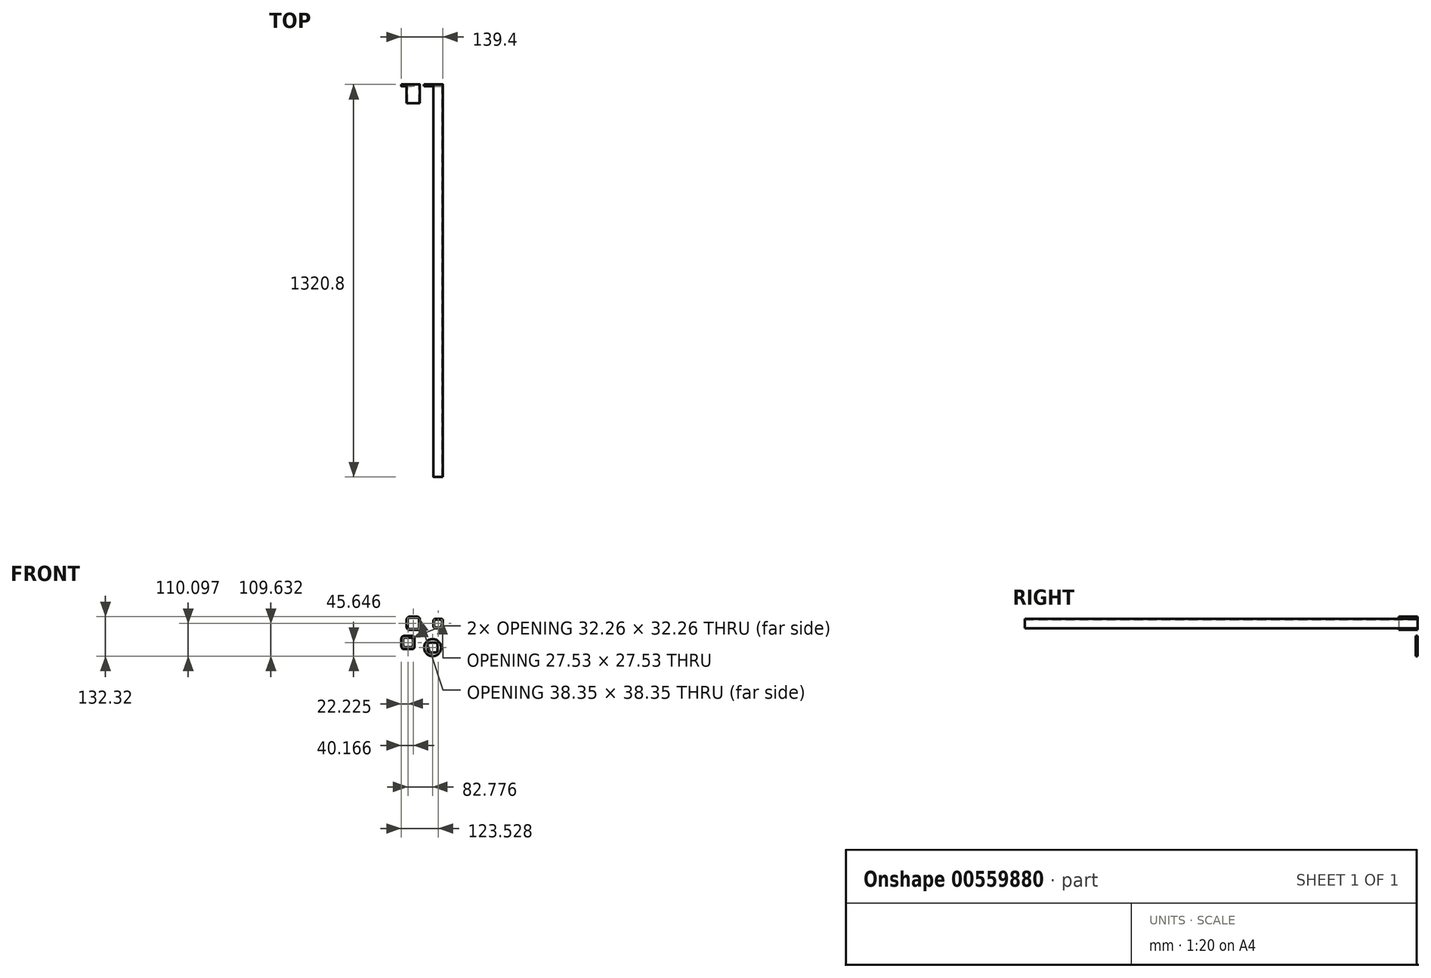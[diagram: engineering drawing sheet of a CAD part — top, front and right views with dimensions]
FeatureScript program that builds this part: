
annotation { "Feature Type Name" : "Feature", "Feature Type Description" : "" }
export const myFeature = defineFeature(function(context is Context, id is Id, definition is map)
    precondition{}
    {
        {
            var Q0;
            Q0=qCreatedBy(makeId("Front.planeOp"),FACE);
            var sketch = newSketch(context, id + "F0", { "sketchPlane" : qUnion([Q0])});
            skLineSegment(sketch, "E0.bottom", {"start": v(-62.7, 67.52) * mm, "end": v(-36.53, 67.52) * mm});
            skLineSegment(sketch, "E0.top", {"start": v(-62.7, 23.07) * mm, "end": v(-36.53, 23.07) * mm});
            skLineSegment(sketch, "E0.left", {"start": v(-71.84, 58.38) * mm, "end": v(-71.84, 32.22) * mm});
            skLineSegment(sketch, "E0.right", {"start": v(-27.39, 58.38) * mm, "end": v(-27.39, 32.22) * mm});
            skLineSegment(sketch, "E1.0", {"start": v(-62.7, 64.47) * mm, "end": v(-36.53, 64.47) * mm});
            skLineSegment(sketch, "E1.1", {"start": v(-68.8, 58.38) * mm, "end": v(-68.8, 32.22) * mm});
            skLineSegment(sketch, "E1.2", {"start": v(-62.7, 26.12) * mm, "end": v(-36.53, 26.12) * mm});
            skLineSegment(sketch, "E1.3", {"start": v(-30.44, 58.38) * mm, "end": v(-30.44, 32.22) * mm});
            skPoint(sketch, "E2.visualSharp", {"position": v(-71.84, 67.52) * mm});
            skArc(sketch, "E2.filletArc", {"start": v(-62.7, 67.52) * mm, "mid": v(-69.16, 64.84) * mm, "end": v(-71.84, 58.38) * mm});
            skPoint(sketch, "E3.visualSharp", {"position": v(-68.8, 64.47) * mm});
            skArc(sketch, "E4.0", {"start": v(-62.7, 64.47) * mm, "mid": v(-67, 62.69) * mm, "end": v(-68.8, 58.38) * mm});
            skLineSegment(sketch, "E5", {"start": v(-49.61, 26.12) * mm, "end": v(-49.61, 64.47) * mm, "construction": true});
            skLineSegment(sketch, "E6", {"start": v(-30.44, 45.3) * mm, "end": v(-68.8, 45.3) * mm, "construction": true});
            skPoint(sketch, "E6.endSnap0", {"position": v(-68.8, 42.25) * mm});
            skArc(sketch, "E7.MirrorCS", {"start": v(-36.53, 64.47) * mm, "mid": v(-32.22, 62.69) * mm, "end": v(-30.44, 58.38) * mm});
            skArc(sketch, "E8.MirrorCS", {"start": v(-36.53, 67.52) * mm, "mid": v(-30.07, 64.84) * mm, "end": v(-27.39, 58.38) * mm});
            skPoint(sketch, "E9.orphan", {"position": v(-30.44, 64.47) * mm});
            skArc(sketch, "E10.MirrorCS", {"start": v(-36.53, 26.12) * mm, "mid": v(-32.22, 27.9) * mm, "end": v(-30.44, 32.22) * mm});
            skArc(sketch, "E11.MirrorCS", {"start": v(-36.53, 23.07) * mm, "mid": v(-30.07, 25.75) * mm, "end": v(-27.39, 32.22) * mm});
            skArc(sketch, "E12.MirrorCS", {"start": v(-62.7, 23.07) * mm, "mid": v(-69.16, 25.75) * mm, "end": v(-71.84, 32.22) * mm});
            skArc(sketch, "E13.MirrorCS", {"start": v(-62.7, 26.12) * mm, "mid": v(-67, 27.9) * mm, "end": v(-68.8, 32.22) * mm});
            skPoint(sketch, "E14.orphan", {"position": v(-71.84, 23.07) * mm});
            skPoint(sketch, "E15.orphan", {"position": v(-68.8, 26.12) * mm});
            skPoint(sketch, "E16.orphan", {"position": v(-30.44, 26.12) * mm});
            skSolve(sketch);
        }
        {
            var Q0;
            Q0=makeQuery(id+"F0.imprint","IMPRINT",FACE,{"disambiguationData":[TD([[makeQuery(id+"F0.imprint","IMPRINT",EDGE,{"derivedFrom":sQuery(id+"F0.wireOp",EDGE,"E0.bottom")}),-1.0]])]});
            extrude(context, id + "F1", {"entities" : qUnion([Q0]), "depth" : 63.5 * mm, "offsetDistance" : 25.4 * mm});
        }
        {
            var Q0;
            Q0=qCreatedBy(makeId("Front.planeOp"),FACE);
            var sketch = newSketch(context, id + "F2", { "sketchPlane" : qUnion([Q0])});
            skLineSegment(sketch, "E17.bottom", {"start": v(24.2, 60.7) * mm, "end": v(43.3, 60.7) * mm});
            skLineSegment(sketch, "E17.top", {"start": v(24.2, 28.96) * mm, "end": v(43.3, 28.96) * mm});
            skLineSegment(sketch, "E17.left", {"start": v(17.87, 54.38) * mm, "end": v(17.87, 35.28) * mm});
            skLineSegment(sketch, "E17.right", {"start": v(49.62, 54.38) * mm, "end": v(49.62, 35.28) * mm});
            skPoint(sketch, "E18.visualSharp", {"position": v(17.87, 60.7) * mm});
            skArc(sketch, "E18.filletArc", {"start": v(24.2, 60.7) * mm, "mid": v(19.73, 58.85) * mm, "end": v(17.87, 54.38) * mm});
            skPoint(sketch, "E19.visualSharp", {"position": v(49.62, 60.7) * mm});
            skArc(sketch, "E19.filletArc", {"start": v(49.62, 54.38) * mm, "mid": v(47.77, 58.85) * mm, "end": v(43.3, 60.7) * mm});
            skPoint(sketch, "E20.visualSharp", {"position": v(49.62, 28.96) * mm});
            skArc(sketch, "E20.filletArc", {"start": v(43.3, 28.96) * mm, "mid": v(47.77, 30.8) * mm, "end": v(49.62, 35.28) * mm});
            skPoint(sketch, "E21.visualSharp", {"position": v(17.87, 28.96) * mm});
            skArc(sketch, "E21.filletArc", {"start": v(17.87, 35.28) * mm, "mid": v(19.73, 30.8) * mm, "end": v(24.2, 28.96) * mm});
            skLineSegment(sketch, "E22.0", {"start": v(24.2, 58.6) * mm, "end": v(43.3, 58.6) * mm});
            skArc(sketch, "E22.1", {"start": v(47.51, 54.38) * mm, "mid": v(46.28, 57.36) * mm, "end": v(43.3, 58.6) * mm});
            skArc(sketch, "E22.2", {"start": v(24.2, 58.6) * mm, "mid": v(21.22, 57.36) * mm, "end": v(19.98, 54.38) * mm});
            skLineSegment(sketch, "E22.3", {"start": v(47.51, 54.38) * mm, "end": v(47.51, 35.28) * mm});
            skLineSegment(sketch, "E22.4", {"start": v(19.98, 54.38) * mm, "end": v(19.98, 35.28) * mm});
            skArc(sketch, "E22.5", {"start": v(19.98, 35.28) * mm, "mid": v(21.22, 32.3) * mm, "end": v(24.2, 31.07) * mm});
            skLineSegment(sketch, "E22.6", {"start": v(24.2, 31.07) * mm, "end": v(43.3, 31.07) * mm});
            skArc(sketch, "E22.7", {"start": v(43.3, 31.07) * mm, "mid": v(46.28, 32.3) * mm, "end": v(47.51, 35.28) * mm});
            skSolve(sketch);
        }
        {
            var Q0;
            Q0=makeQuery(id+"F2.imprint","IMPRINT",FACE,{"disambiguationData":[TD([[makeQuery(id+"F2.imprint","IMPRINT",EDGE,{"derivedFrom":sQuery(id+"F2.wireOp",EDGE,"E17.bottom")}),-1.0]])]});
            extrude(context, id + "F3", {"entities" : qUnion([Q0]), "depth" : 1320.8 * mm, "offsetDistance" : 25.4 * mm});
        }
        {
            var Q0;
            Q0=qCreatedBy(makeId("Front.planeOp"),FACE);
            var sketch = newSketch(context, id + "F4", { "sketchPlane" : qUnion([Q0])});
            skPoint(sketch, "E23.visualSharp", {"position": v(-89.78, 2.96) * mm});
            skPoint(sketch, "E24.visualSharp", {"position": v(-87.62, 0.91) * mm});
            skLineSegment(sketch, "E25", {"start": v(-67.55, -39.22) * mm, "end": v(-67.55, 0.91) * mm, "construction": true});
            skLineSegment(sketch, "E26", {"start": v(-47.49, -19.15) * mm, "end": v(-87.62, -19.15) * mm, "construction": true});
            skPoint(sketch, "E26.endSnap0", {"position": v(-87.62, -23.3) * mm});
            skPoint(sketch, "E27.orphan", {"position": v(-47.49, 0.91) * mm});
            skPoint(sketch, "E28.orphan", {"position": v(-89.78, -41.5) * mm});
            skPoint(sketch, "E29.orphan", {"position": v(-87.62, -39.22) * mm});
            skPoint(sketch, "E30.orphan", {"position": v(-47.49, -39.22) * mm});
            skLineSegment(sketch, "E31.bottom", {"start": v(-77.1, -3.28) * mm, "end": v(-58, -3.28) * mm, "construction": true});
            skLineSegment(sketch, "E31.top", {"start": v(-77.1, -35.03) * mm, "end": v(-58, -35.03) * mm, "construction": true});
            skLineSegment(sketch, "E31.left", {"start": v(-83.43, -9.6) * mm, "end": v(-83.43, -28.7) * mm, "construction": true});
            skLineSegment(sketch, "E31.right", {"start": v(-51.68, -9.6) * mm, "end": v(-51.68, -28.7) * mm, "construction": true});
            skPoint(sketch, "E32.visualSharp", {"position": v(-83.43, -3.28) * mm});
            skArc(sketch, "E32.filletArc", {"start": v(-77.1, -3.28) * mm, "mid": v(-81.58, -5.13) * mm, "end": v(-83.43, -9.6) * mm, "construction": true});
            skPoint(sketch, "E33.visualSharp", {"position": v(-51.68, -3.28) * mm});
            skArc(sketch, "E33.filletArc", {"start": v(-51.68, -9.6) * mm, "mid": v(-53.53, -5.13) * mm, "end": v(-58, -3.28) * mm, "construction": true});
            skPoint(sketch, "E34.visualSharp", {"position": v(-51.68, -35.03) * mm});
            skArc(sketch, "E34.filletArc", {"start": v(-58, -35.03) * mm, "mid": v(-53.53, -33.18) * mm, "end": v(-51.68, -28.7) * mm, "construction": true});
            skPoint(sketch, "E35.visualSharp", {"position": v(-83.43, -35.03) * mm});
            skArc(sketch, "E35.filletArc", {"start": v(-83.43, -28.7) * mm, "mid": v(-81.58, -33.18) * mm, "end": v(-77.1, -35.03) * mm, "construction": true});
            skLineSegment(sketch, "E36", {"start": v(-51.68, -19.15) * mm, "end": v(-83.43, -19.15) * mm, "construction": true});
            skLineSegment(sketch, "E37", {"start": v(-67.55, -3.28) * mm, "end": v(-67.55, -35.03) * mm, "construction": true});
            skArc(sketch, "E38.0", {"start": v(-77.1, -3.02) * mm, "mid": v(-81.76, -4.95) * mm, "end": v(-83.68, -9.6) * mm});
            skLineSegment(sketch, "E38.1", {"start": v(-83.68, -9.6) * mm, "end": v(-83.68, -28.7) * mm});
            skLineSegment(sketch, "E38.2", {"start": v(-77.1, -3.02) * mm, "end": v(-58, -3.02) * mm});
            skArc(sketch, "E38.3", {"start": v(-83.68, -28.7) * mm, "mid": v(-81.76, -33.36) * mm, "end": v(-77.1, -35.28) * mm});
            skArc(sketch, "E38.4", {"start": v(-51.43, -9.6) * mm, "mid": v(-53.35, -4.95) * mm, "end": v(-58, -3.02) * mm});
            skLineSegment(sketch, "E38.5", {"start": v(-51.43, -9.6) * mm, "end": v(-51.43, -28.7) * mm});
            skArc(sketch, "E38.6", {"start": v(-58, -35.28) * mm, "mid": v(-53.35, -33.36) * mm, "end": v(-51.43, -28.7) * mm});
            skLineSegment(sketch, "E38.7", {"start": v(-77.1, -35.28) * mm, "end": v(-58, -35.28) * mm});
            skLineSegment(sketch, "E39.bottom", {"start": v(-80.64, 3.07) * mm, "end": v(-54.47, 3.07) * mm});
            skLineSegment(sketch, "E39.top", {"start": v(-80.64, -41.38) * mm, "end": v(-54.47, -41.38) * mm});
            skLineSegment(sketch, "E39.left", {"start": v(-89.78, -6.07) * mm, "end": v(-89.78, -32.23) * mm});
            skLineSegment(sketch, "E39.right", {"start": v(-45.33, -6.07) * mm, "end": v(-45.33, -32.23) * mm});
            skLineSegment(sketch, "E40.0", {"start": v(-80.64, 0.02) * mm, "end": v(-54.47, 0.02) * mm, "construction": true});
            skLineSegment(sketch, "E40.1", {"start": v(-86.73, -6.07) * mm, "end": v(-86.73, -32.23) * mm, "construction": true});
            skLineSegment(sketch, "E40.2", {"start": v(-80.64, -38.33) * mm, "end": v(-54.47, -38.33) * mm, "construction": true});
            skLineSegment(sketch, "E40.3", {"start": v(-48.38, -6.07) * mm, "end": v(-48.38, -32.23) * mm, "construction": true});
            skPoint(sketch, "E41.visualSharp", {"position": v(-89.78, 3.07) * mm});
            skArc(sketch, "E41.filletArc", {"start": v(-80.64, 3.07) * mm, "mid": v(-87.1, 0.4) * mm, "end": v(-89.78, -6.07) * mm});
            skPoint(sketch, "E42.visualSharp", {"position": v(-86.73, 0.02) * mm});
            skArc(sketch, "E43.0", {"start": v(-80.64, 0.02) * mm, "mid": v(-84.95, -1.76) * mm, "end": v(-86.73, -6.07) * mm, "construction": true});
            skLineSegment(sketch, "E44", {"start": v(-67.55, -38.33) * mm, "end": v(-67.55, 0.02) * mm, "construction": true});
            skLineSegment(sketch, "E45", {"start": v(-48.38, -19.15) * mm, "end": v(-86.73, -19.15) * mm, "construction": true});
            skPoint(sketch, "E45.endSnap0", {"position": v(-86.73, -22.2) * mm});
            skArc(sketch, "E46.MirrorCS", {"start": v(-54.47, 0.02) * mm, "mid": v(-50.16, -1.76) * mm, "end": v(-48.38, -6.07) * mm, "construction": true});
            skArc(sketch, "E47.MirrorCS", {"start": v(-54.47, 3.07) * mm, "mid": v(-48, 0.4) * mm, "end": v(-45.33, -6.07) * mm});
            skPoint(sketch, "E48.orphan", {"position": v(-48.38, 0.02) * mm});
            skArc(sketch, "E49.MirrorCS", {"start": v(-54.47, -38.33) * mm, "mid": v(-50.16, -36.55) * mm, "end": v(-48.38, -32.23) * mm, "construction": true});
            skArc(sketch, "E50.MirrorCS", {"start": v(-54.47, -41.38) * mm, "mid": v(-48, -38.7) * mm, "end": v(-45.33, -32.23) * mm});
            skArc(sketch, "E51.MirrorCS", {"start": v(-80.64, -41.38) * mm, "mid": v(-87.1, -38.7) * mm, "end": v(-89.78, -32.23) * mm});
            skArc(sketch, "E52.MirrorCS", {"start": v(-80.64, -38.33) * mm, "mid": v(-84.95, -36.55) * mm, "end": v(-86.73, -32.23) * mm, "construction": true});
            skPoint(sketch, "E53.orphan", {"position": v(-89.78, -41.38) * mm});
            skPoint(sketch, "E54.orphan", {"position": v(-86.73, -38.33) * mm});
            skPoint(sketch, "E55.orphan", {"position": v(-48.38, -38.33) * mm});
            skSolve(sketch);
        }
        {
            var Q0;
            Q0=makeQuery(id+"F4.imprint","IMPRINT",FACE,{"disambiguationData":[TD([[makeQuery(id+"F4.imprint","IMPRINT",EDGE,{"derivedFrom":sQuery(id+"F4.wireOp",EDGE,"E38.0")}),-1.0]])]});
            extrude(context, id + "F5", {"entities" : qUnion([Q0]), "depth" : 6.35 * mm, "offsetDistance" : 25.4 * mm});
        }
        {
            var Q0;
            Q0=qCreatedBy(makeId("Front.planeOp"),FACE);
            var sketch = newSketch(context, id + "F6", { "sketchPlane" : qUnion([Q0])});
            skLineSegment(sketch, "E56.bottom", {"start": v(2.14, -14) * mm, "end": v(28.3, -14) * mm, "construction": true});
            skLineSegment(sketch, "E56.top", {"start": v(2.14, -58.45) * mm, "end": v(28.3, -58.45) * mm, "construction": true});
            skLineSegment(sketch, "E56.left", {"start": v(-7, -23.15) * mm, "end": v(-7, -49.3) * mm, "construction": true});
            skLineSegment(sketch, "E56.right", {"start": v(37.45, -23.15) * mm, "end": v(37.45, -49.3) * mm, "construction": true});
            skPoint(sketch, "E57.visualSharp", {"position": v(-7, -14) * mm});
            skArc(sketch, "E57.filletArc", {"start": v(2.14, -14) * mm, "mid": v(-4.33, -16.68) * mm, "end": v(-7, -23.15) * mm, "construction": true});
            skPoint(sketch, "E58.visualSharp", {"position": v(-3.96, -17.05) * mm});
            skLineSegment(sketch, "E59", {"start": v(15.22, -55.4) * mm, "end": v(15.22, -17.05) * mm, "construction": true});
            skLineSegment(sketch, "E60", {"start": v(34.4, -36.23) * mm, "end": v(-3.96, -36.23) * mm, "construction": true});
            skPoint(sketch, "E60.endSnap0", {"position": v(-3.96, -39.27) * mm});
            skArc(sketch, "E61.MirrorCS", {"start": v(28.3, -14) * mm, "mid": v(34.77, -16.68) * mm, "end": v(37.45, -23.15) * mm, "construction": true});
            skPoint(sketch, "E62.orphan", {"position": v(34.4, -17.05) * mm});
            skArc(sketch, "E63.MirrorCS", {"start": v(28.3, -58.45) * mm, "mid": v(34.77, -55.77) * mm, "end": v(37.45, -49.3) * mm, "construction": true});
            skArc(sketch, "E64.MirrorCS", {"start": v(2.14, -58.45) * mm, "mid": v(-4.33, -55.77) * mm, "end": v(-7, -49.3) * mm, "construction": true});
            skPoint(sketch, "E65.orphan", {"position": v(-7, -58.45) * mm});
            skPoint(sketch, "E66.orphan", {"position": v(-3.96, -55.4) * mm});
            skPoint(sketch, "E67.orphan", {"position": v(34.4, -55.4) * mm});
            skCircle(sketch, "E68", {"center": v(15.22, -36.23) * mm, "radius": 28.58 * mm});
            skLineSegment(sketch, "E69.bottom", {"start": v(5.67, -20.35) * mm, "end": v(24.77, -20.35) * mm, "construction": true});
            skLineSegment(sketch, "E69.top", {"start": v(5.67, -52.1) * mm, "end": v(24.77, -52.1) * mm, "construction": true});
            skLineSegment(sketch, "E69.left", {"start": v(-0.65, -26.68) * mm, "end": v(-0.65, -45.78) * mm, "construction": true});
            skLineSegment(sketch, "E69.right", {"start": v(31.1, -26.68) * mm, "end": v(31.1, -45.78) * mm, "construction": true});
            skArc(sketch, "E70.filletArc", {"start": v(5.67, -20.35) * mm, "mid": v(1.2, -22.2) * mm, "end": v(-0.65, -26.68) * mm, "construction": true});
            skArc(sketch, "E71.filletArc", {"start": v(31.1, -26.68) * mm, "mid": v(29.24, -22.2) * mm, "end": v(24.77, -20.35) * mm, "construction": true});
            skArc(sketch, "E72.filletArc", {"start": v(24.77, -52.1) * mm, "mid": v(29.24, -50.25) * mm, "end": v(31.1, -45.78) * mm, "construction": true});
            skArc(sketch, "E73.filletArc", {"start": v(-0.65, -45.78) * mm, "mid": v(1.2, -50.25) * mm, "end": v(5.67, -52.1) * mm, "construction": true});
            skArc(sketch, "E74.0", {"start": v(5.67, -20.1) * mm, "mid": v(1.02, -22.02) * mm, "end": v(-0.9, -26.68) * mm});
            skLineSegment(sketch, "E74.1", {"start": v(-0.9, -26.68) * mm, "end": v(-0.9, -45.78) * mm});
            skLineSegment(sketch, "E74.2", {"start": v(5.67, -20.1) * mm, "end": v(24.77, -20.1) * mm});
            skArc(sketch, "E74.3", {"start": v(-0.9, -45.78) * mm, "mid": v(1.02, -50.43) * mm, "end": v(5.67, -52.36) * mm});
            skArc(sketch, "E74.4", {"start": v(31.35, -26.68) * mm, "mid": v(29.42, -22.02) * mm, "end": v(24.77, -20.1) * mm});
            skLineSegment(sketch, "E74.5", {"start": v(31.35, -26.68) * mm, "end": v(31.35, -45.78) * mm});
            skArc(sketch, "E74.6", {"start": v(24.77, -52.36) * mm, "mid": v(29.42, -50.43) * mm, "end": v(31.35, -45.78) * mm});
            skLineSegment(sketch, "E74.7", {"start": v(5.67, -52.36) * mm, "end": v(24.77, -52.36) * mm});
            skSolve(sketch);
        }
        {
            var Q0;
            Q0=makeQuery(id+"F6.imprint","IMPRINT",FACE,{"disambiguationData":[TD([[makeQuery(id+"F6.imprint","IMPRINT",EDGE,{"derivedFrom":sQuery(id+"F6.wireOp",EDGE,"E68")}),1.0]])]});
            extrude(context, id + "F7", {"entities" : qUnion([Q0]), "depth" : 6.35 * mm, "offsetDistance" : 25.4 * mm});
        }
    });
